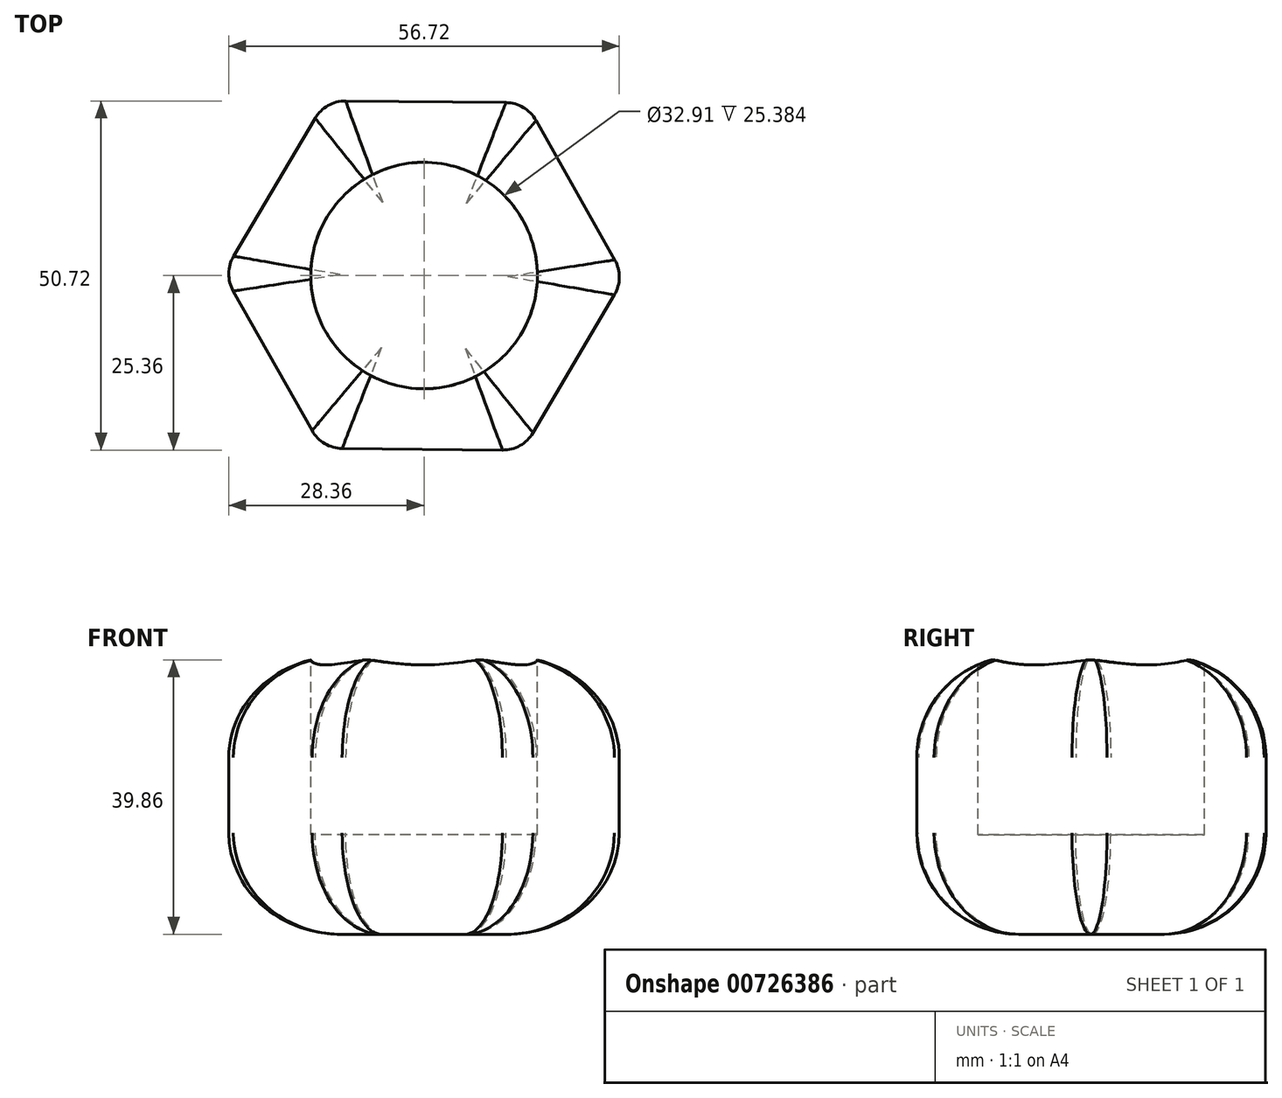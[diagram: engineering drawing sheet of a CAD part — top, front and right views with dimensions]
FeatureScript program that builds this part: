
annotation { "Feature Type Name" : "Feature", "Feature Type Description" : "" }
export const myFeature = defineFeature(function(context is Context, id is Id, definition is map)
    precondition{}
    {
        {
            var Q0;
            Q0=qCreatedBy(makeId("Top.planeOp"),FACE);
            var sketch = newSketch(context, id + "F0", { "sketchPlane" : qUnion([Q0])});
            skCircle(sketch, "E0.cCircle", {"center": v(0, 0) * mm, "radius": 25.25 * mm, "construction": true});
            skLineSegment(sketch, "E0.0", {"start": v(14.82, 25.1) * mm, "end": v(29.15, -0.29) * mm});
            skLineSegment(sketch, "E0.1", {"start": v(29.15, -0.29) * mm, "end": v(14.33, -25.39) * mm});
            skLineSegment(sketch, "E0.2", {"start": v(14.33, -25.39) * mm, "end": v(-14.82, -25.1) * mm});
            skLineSegment(sketch, "E0.3", {"start": v(-14.82, -25.1) * mm, "end": v(-29.15, 0.29) * mm});
            skLineSegment(sketch, "E0.4", {"start": v(-29.15, 0.29) * mm, "end": v(-14.33, 25.39) * mm});
            skLineSegment(sketch, "E0.5", {"start": v(-14.33, 25.39) * mm, "end": v(14.82, 25.1) * mm});
            skPoint(sketch, "E0.0.midPoint", {"position": v(21.99, 12.4) * mm});
            skSolve(sketch);
        }
        {
            var Q0;
            Q0=makeQuery(id+"F0.imprint","IMPRINT",FACE,{"disambiguationData":[TD([[makeQuery(id+"F0.imprint","IMPRINT",EDGE,{"derivedFrom":sQuery(id+"F0.wireOp",EDGE,"E0.0")}),-1.0]])]});
            extrude(context, id + "F1", {"entities" : qUnion([Q0]), "depth" : 40.4 * mm, "offsetDistance" : 25.4 * mm});
        }
        {
            var Q0;
            Q0=makeQuery(id+"F1.opExtrude","CAP_EDGE",EDGE,{"disambiguationData":[OSD([sQuery(id+"F0.wireOp",EDGE,"E0.4")])],"isStart":false});
            var Q1;
            Q1=makeQuery(id+"F1.opExtrude","CAP_EDGE",EDGE,{"disambiguationData":[OSD([sQuery(id+"F0.wireOp",EDGE,"E0.3")])],"isStart":false});
            var Q2;
            Q2=makeQuery(id+"F1.opExtrude","CAP_EDGE",EDGE,{"disambiguationData":[OSD([sQuery(id+"F0.wireOp",EDGE,"E0.2")])],"isStart":false});
            var Q3;
            Q3=makeQuery(id+"F1.opExtrude","CAP_EDGE",EDGE,{"disambiguationData":[OSD([sQuery(id+"F0.wireOp",EDGE,"E0.1")])],"isStart":false});
            var Q4;
            Q4=makeQuery(id+"F1.opExtrude","CAP_EDGE",EDGE,{"disambiguationData":[OSD([sQuery(id+"F0.wireOp",EDGE,"E0.0")])],"isStart":false});
            var Q5;
            Q5=makeQuery(id+"F1.opExtrude","CAP_EDGE",EDGE,{"disambiguationData":[OSD([sQuery(id+"F0.wireOp",EDGE,"E0.5")])],"isStart":false});
            var Q6;
            Q6=makeQuery(id+"F1.opExtrude","CAP_EDGE",EDGE,{"disambiguationData":[OSD([sQuery(id+"F0.wireOp",EDGE,"E0.3")])],"isStart":true});
            var Q7;
            Q7=makeQuery(id+"F1.opExtrude","CAP_EDGE",EDGE,{"disambiguationData":[OSD([sQuery(id+"F0.wireOp",EDGE,"E0.4")])],"isStart":true});
            var Q8;
            Q8=makeQuery(id+"F1.opExtrude","CAP_EDGE",EDGE,{"disambiguationData":[OSD([sQuery(id+"F0.wireOp",EDGE,"E0.2")])],"isStart":true});
            var Q9;
            Q9=makeQuery(id+"F1.opExtrude","CAP_EDGE",EDGE,{"disambiguationData":[OSD([sQuery(id+"F0.wireOp",EDGE,"E0.1")])],"isStart":true});
            var Q10;
            Q10=makeQuery(id+"F1.opExtrude","CAP_EDGE",EDGE,{"disambiguationData":[OSD([sQuery(id+"F0.wireOp",EDGE,"E0.0")])],"isStart":true});
            var Q11;
            Q11=makeQuery(id+"F1.opExtrude","CAP_EDGE",EDGE,{"disambiguationData":[OSD([sQuery(id+"F0.wireOp",EDGE,"E0.5")])],"isStart":true});
            fillet(context, id + "F2", {"entities" : qUnion([Q0, Q1, Q2, Q3, Q4, Q5, Q6, Q7, Q8, Q9, Q10, Q11]), "radius" : 14.72 * mm, "tangentPropagation" : true, "allowEdgeOverflow" : false});
        }
        {
            var Q0;
            Q0=makeQuery(id+"F1.opExtrude","SWEPT_EDGE",EDGE,{"disambiguationData":[OSD([sQuery(id+"F0.wireOp",EDGE,"E0.0"),sQuery(id+"F0.wireOp",EDGE,"E0.1")])]});
            var Q1;
            Q1=makeQuery(id+"F1.opExtrude","SWEPT_EDGE",EDGE,{"disambiguationData":[OSD([sQuery(id+"F0.wireOp",EDGE,"E0.1"),sQuery(id+"F0.wireOp",EDGE,"E0.2")])]});
            var Q2;
            Q2=makeQuery(id+"F1.opExtrude","SWEPT_EDGE",EDGE,{"disambiguationData":[OSD([sQuery(id+"F0.wireOp",EDGE,"E0.2"),sQuery(id+"F0.wireOp",EDGE,"E0.3")])]});
            var Q3;
            Q3=makeQuery(id+"F1.opExtrude","SWEPT_FACE",FACE,{"disambiguationData":[OSD([sQuery(id+"F0.wireOp",EDGE,"E0.3")])]});
            var Q4;
            Q4=makeQuery(id+"F1.opExtrude","SWEPT_EDGE",EDGE,{"disambiguationData":[OSD([sQuery(id+"F0.wireOp",EDGE,"E0.4"),sQuery(id+"F0.wireOp",EDGE,"E0.5")])]});
            var Q5;
            Q5=makeQuery(id+"F1.opExtrude","SWEPT_EDGE",EDGE,{"disambiguationData":[OSD([sQuery(id+"F0.wireOp",EDGE,"E0.0"),sQuery(id+"F0.wireOp",EDGE,"E0.5")])]});
            var Q6;
            {var subQ0=sQuery(id+"F0.wireOp",EDGE,"E0.0");Q6=makeQuery(id+"F2.opFillet","BLEND_EDGE",EDGE,{"blendedFrom":[makeQuery(id+"F1.opExtrude","CAP_EDGE",EDGE,{"disambiguationData":[OSD([subQ0])],"isStart":false}),makeQuery(id+"F1.opExtrude","SWEPT_FACE",FACE,{"disambiguationData":[OSD([subQ0])]})],"blendedInto":[makeQuery(id+"F1.opExtrude","SWEPT_FACE",FACE,{"disambiguationData":[OSD([subQ0])]})]});}
            fillet(context, id + "F3", {"entities" : qUnion([Q0, Q1, Q2, Q3, Q4, Q5, Q6]), "radius" : 5.08 * mm, "tangentPropagation" : true, "allowEdgeOverflow" : false});
        }
        {
            var Q0;
            Q0=makeQuery(id+"F1.opExtrude","CAP_FACE",FACE,{"disambiguationData":[OSD([sQuery(id+"F0.wireOp",EDGE,"E0.0"),sQuery(id+"F0.wireOp",EDGE,"E0.1"),sQuery(id+"F0.wireOp",EDGE,"E0.2"),sQuery(id+"F0.wireOp",EDGE,"E0.3"),sQuery(id+"F0.wireOp",EDGE,"E0.4"),sQuery(id+"F0.wireOp",EDGE,"E0.5")])],"isStart":false});
            var sketch = newSketch(context, id + "F4", { "sketchPlane" : qUnion([Q0])});
            skCircle(sketch, "E1", {"center": v(0, 0) * mm, "radius": 16.46 * mm});
            skSolve(sketch);
        }
        {
            var Q0;
            Q0=makeQuery(id+"F4.imprint","IMPRINT",FACE,{"disambiguationData":[TD([[makeQuery(id+"F4.imprint","IMPRINT",EDGE,{"derivedFrom":sQuery(id+"F4.wireOp",EDGE,"E1")}),1.0]])]});
            var Q1;
            {var subQ0=sQuery(id+"F0.wireOp",EDGE,"E0.5");var subQ1=sQuery(id+"F0.wireOp",EDGE,"E0.4");var subQ2=sQuery(id+"F0.wireOp",EDGE,"E0.3");var subQ3=sQuery(id+"F0.wireOp",EDGE,"E0.2");var subQ4=sQuery(id+"F0.wireOp",EDGE,"E0.1");var subQ5=sQuery(id+"F0.wireOp",EDGE,"E0.0");var subQ6=makeQuery(id+"F1.opExtrude","CAP_FACE",FACE,{"disambiguationData":[OSD([subQ5,subQ4,subQ3,subQ2,subQ1,subQ0])],"isStart":false});Q1=makeQuery(id+"F4.imprint","IMPRINT",FACE,{"disambiguationData":[TD([[makeQuery(id+"F4.imprint","IMPRINT",EDGE,{"derivedFrom":makeQuery(id+"F2.opFillet","BLEND_EDGE",EDGE,{"blendedFrom":[makeQuery(id+"F1.opExtrude","CAP_EDGE",EDGE,{"disambiguationData":[OSD([subQ5])],"isStart":false}),subQ6],"blendedInto":[subQ6]})}),1.0]])]});}
            extrude(context, id + "F5", {"entities" : qUnion([Q0, Q1]), "operationType" : NewBodyOperationType.REMOVE, "oppositeDirection" : true, "depth" : 9.14 * mm, "offsetDistance" : 25.4 * mm});
        }
        {
            var Q0;
            Q0=makeQuery(id+"F5.boolean.opBoolean","COPY",FACE,{"derivedFrom":makeQuery(id+"F5.opExtrude","CAP_FACE",FACE,{"disambiguationData":[OSD([sQuery(id+"F4.wireOp",EDGE,"E1")])],"isStart":false})});
            extrude(context, id + "F6", {"entities" : qUnion([Q0]), "operationType" : NewBodyOperationType.REMOVE, "oppositeDirection" : true, "depth" : 16.76 * mm, "offsetDistance" : 25.4 * mm});
        }
    });
